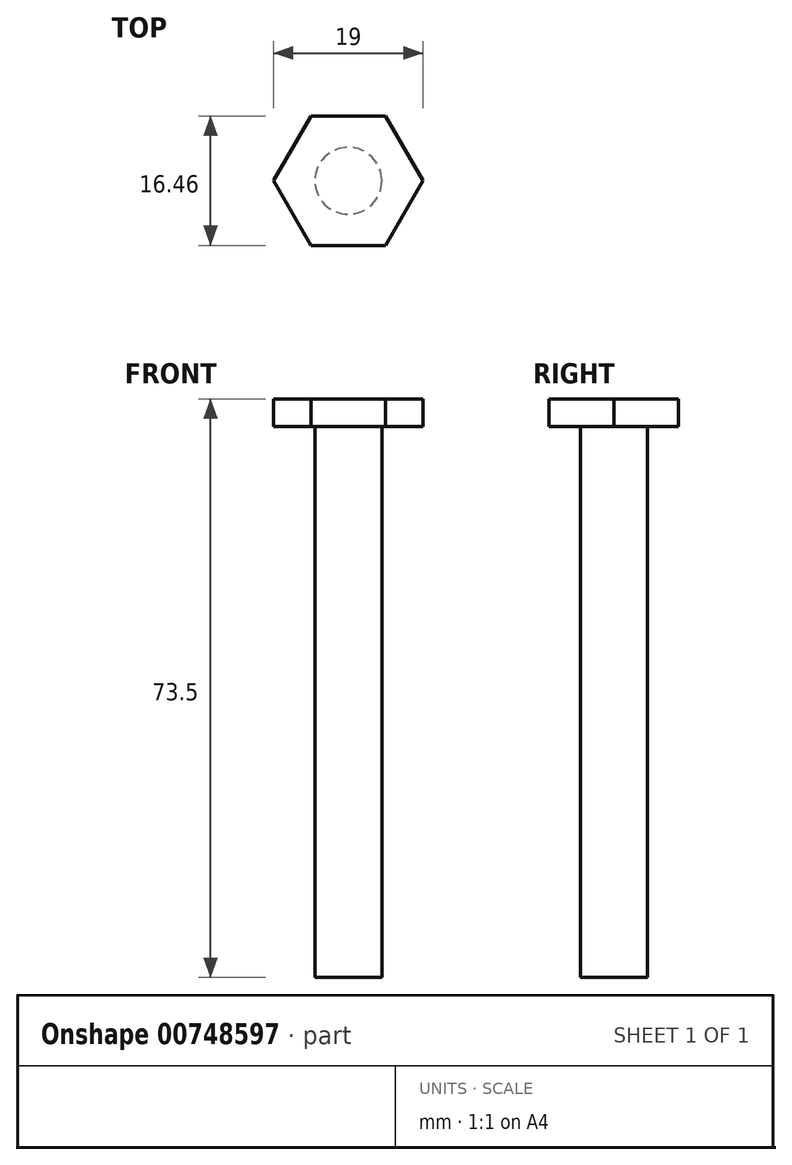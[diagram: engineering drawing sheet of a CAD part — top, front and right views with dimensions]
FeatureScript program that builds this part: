
annotation { "Feature Type Name" : "Feature", "Feature Type Description" : "" }
export const myFeature = defineFeature(function(context is Context, id is Id, definition is map)
    precondition{}
    {
        {
            var Q0;
            Q0=qCreatedBy(makeId("Front.planeOp"),FACE);
            var sketch = newSketch(context, id + "F0", { "sketchPlane" : qUnion([Q0])});
            skLineSegment(sketch, "E0.bottom", {"start": v(4.25, 35) * mm, "end": v(-4.25, 35) * mm});
            skLineSegment(sketch, "E0.top", {"start": v(4.25, -35) * mm, "end": v(-4.25, -35) * mm});
            skLineSegment(sketch, "E0.left", {"start": v(4.25, 35) * mm, "end": v(4.25, -35) * mm});
            skLineSegment(sketch, "E0.right", {"start": v(-4.25, 35) * mm, "end": v(-4.25, -35) * mm});
            skLineSegment(sketch, "E1.bottom", {"start": v(0, 35) * mm, "end": v(9.5, 35) * mm});
            skLineSegment(sketch, "E1.top", {"start": v(0, 38.5) * mm, "end": v(9.5, 38.5) * mm});
            skLineSegment(sketch, "E1.left", {"start": v(0, 35) * mm, "end": v(0, 38.5) * mm});
            skLineSegment(sketch, "E1.right", {"start": v(9.5, 35) * mm, "end": v(9.5, 38.5) * mm});
            skLineSegment(sketch, "E2.MirrorCS", {"start": v(0, 38.5) * mm, "end": v(-9.5, 38.5) * mm});
            skLineSegment(sketch, "E3.MirrorCS", {"start": v(-9.5, 35) * mm, "end": v(-9.5, 38.5) * mm});
            skLineSegment(sketch, "E4.MirrorCS", {"start": v(0, 35) * mm, "end": v(-9.5, 35) * mm});
            skLineSegment(sketch, "E5.bottom", {"start": v(-4.25, -35) * mm, "end": v(4.25, -35) * mm});
            skLineSegment(sketch, "E5.top", {"start": v(-4.25, -1) * mm, "end": v(4.25, -1) * mm});
            skLineSegment(sketch, "E5.left", {"start": v(-4.25, -35) * mm, "end": v(-4.25, -1) * mm});
            skLineSegment(sketch, "E5.right", {"start": v(4.25, -35) * mm, "end": v(4.25, -1) * mm});
            skLineSegment(sketch, "E6", {"start": v(0, 35) * mm, "end": v(0, -35) * mm});
            skLineSegment(sketch, "E7", {"start": v(7.5, 38.5) * mm, "end": v(7.5, 35) * mm});
            skLineSegment(sketch, "E8.MirrorCS", {"start": v(-7.5, 38.5) * mm, "end": v(-7.5, 35) * mm});
            skSolve(sketch);
        }
        {
            var Q0;
            {var subQ4=sQuery(id+"F0.wireOp",EDGE,"E1.left");Q0=makeQuery(id+"F0.imprint","IMPRINT",FACE,{"disambiguationData":[TD([[makeQuery(id+"F0.imprint","IMPRINT",EDGE,{"derivedFrom":subQ4}),1.0]])]});}
            var Q1;
            {var subQ0=sQuery(id+"F0.wireOp",EDGE,"E3.MirrorCS");Q1=makeQuery(id+"F0.imprint","IMPRINT",FACE,{"disambiguationData":[TD([[makeQuery(id+"F0.imprint","IMPRINT",EDGE,{"derivedFrom":subQ0}),-1.0]])]});}
            var Q2;
            {var subQ0=sQuery(id+"F0.wireOp",EDGE,"E0.right");Q2=makeQuery(id+"F0.imprint","IMPRINT",FACE,{"disambiguationData":[TD([[makeQuery(id+"F0.imprint","IMPRINT",EDGE,{"derivedFrom":subQ0}),1.0]])]});}
            var Q3;
            {var subQ0=sQuery(id+"F0.wireOp",EDGE,"E5.left");Q3=makeQuery(id+"F0.imprint","IMPRINT",FACE,{"disambiguationData":[TD([[makeQuery(id+"F0.imprint","IMPRINT",EDGE,{"derivedFrom":subQ0}),-1.0]])]});}
            var Q4;
            Q4=sQuery(id+"F0.wireOp",EDGE,"E1.left");
            revolve(context, id + "F1", {"surfaceOperationType" : NewSurfaceOperationType.NEW, "entities" : qUnion([Q0, Q1, Q2, Q3]), "axis" : qUnion([Q4]), "revolveType" : RevolveType.FULL});
        }
        {
            var Q0;
            Q0=makeQuery(id+"F1.opRevolve","SWEPT_FACE",FACE,{"disambiguationData":[OSD([sQuery(id+"F0.wireOp",EDGE,"E2.MirrorCS")])]});
            var sketch = newSketch(context, id + "F2", { "sketchPlane" : qUnion([Q0])});
            skCircle(sketch, "E9.cCircle", {"center": v(0, 0) * mm, "radius": 9.5 * mm, "construction": true});
            skLineSegment(sketch, "E9.0", {"start": v(9.5, 0) * mm, "end": v(4.75, -8.23) * mm});
            skLineSegment(sketch, "E9.1", {"start": v(4.75, -8.23) * mm, "end": v(-4.75, -8.23) * mm});
            skLineSegment(sketch, "E9.2", {"start": v(-4.75, -8.23) * mm, "end": v(-9.5, 0) * mm});
            skLineSegment(sketch, "E9.3", {"start": v(-9.5, 0) * mm, "end": v(-4.75, 8.23) * mm});
            skLineSegment(sketch, "E9.4", {"start": v(-4.75, 8.23) * mm, "end": v(4.75, 8.23) * mm});
            skLineSegment(sketch, "E9.5", {"start": v(4.75, 8.23) * mm, "end": v(9.5, 0) * mm});
            skSolve(sketch);
        }
        {
            var Q0;
            Q0=makeQuery(id+"F2.imprint","IMPRINT",FACE,{"disambiguationData":[TD([[makeQuery(id+"F2.imprint","IMPRINT",EDGE,{"derivedFrom":sQuery(id+"F2.wireOp",EDGE,"E9.0")}),-1.0]])]});
            extrude(context, id + "F3", {"entities" : qUnion([Q0]), "operationType" : NewBodyOperationType.INTERSECT, "endBound" : BoundingType.UP_TO_NEXT, "oppositeDirection" : true, "depth" : 25 * mm, "offsetDistance" : 25 * mm});
        }
    });
